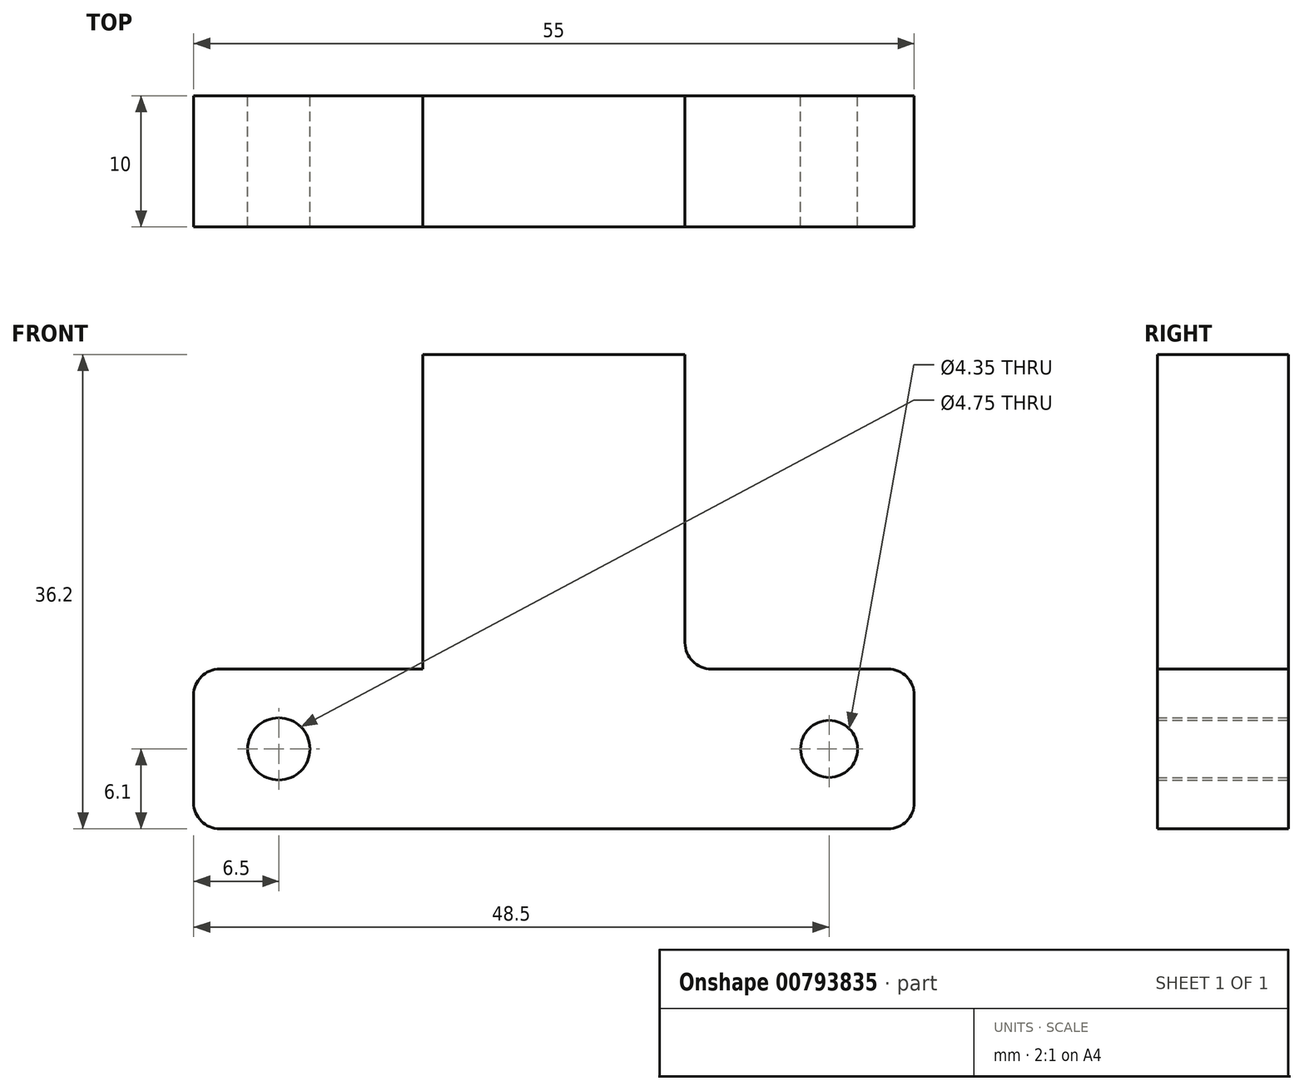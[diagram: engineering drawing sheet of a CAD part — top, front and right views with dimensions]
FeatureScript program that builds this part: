
annotation { "Feature Type Name" : "Feature", "Feature Type Description" : "" }
export const myFeature = defineFeature(function(context is Context, id is Id, definition is map)
    precondition{}
    {
        {
            var Q0;
            Q0=qCreatedBy(makeId("Front.planeOp"),FACE);
            var sketch = newSketch(context, id + "F0", { "sketchPlane" : qUnion([Q0])});
            skLineSegment(sketch, "E0.bottom", {"start": v(-27.5, 6.1) * mm, "end": v(27.5, 6.1) * mm});
            skLineSegment(sketch, "E0.top", {"start": v(-27.5, -6.1) * mm, "end": v(27.5, -6.1) * mm});
            skLineSegment(sketch, "E0.left", {"start": v(-27.5, 6.1) * mm, "end": v(-27.5, -6.1) * mm});
            skLineSegment(sketch, "E0.right", {"start": v(27.5, 6.1) * mm, "end": v(27.5, -6.1) * mm});
            skCircle(sketch, "E1", {"center": v(21, 0) * mm, "radius": 2.18 * mm});
            skCircle(sketch, "E2", {"center": v(-21, 0) * mm, "radius": 2.37 * mm});
            skSolve(sketch);
        }
        {
            var Q0;
            Q0=qSketchRegion(id+"F0",true);
            extrude(context, id + "F1", {"entities" : qUnion([Q0]), "depth" : 10 * mm, "offsetDistance" : 25 * mm});
        }
        {
            var Q0;
            Q0=makeQuery(id+"F1.opExtrude","SWEPT_FACE",FACE,{"disambiguationData":[OSD([sQuery(id+"F0.wireOp",EDGE,"E0.bottom")])]});
            var sketch = newSketch(context, id + "F2", { "sketchPlane" : qUnion([Q0])});
            skLineSegment(sketch, "E3.bottom", {"start": v(-10, 0) * mm, "end": v(10, 0) * mm});
            skLineSegment(sketch, "E3.top", {"start": v(-10, -10) * mm, "end": v(10, -10) * mm});
            skLineSegment(sketch, "E3.left", {"start": v(-10, 0) * mm, "end": v(-10, -10) * mm});
            skLineSegment(sketch, "E3.right", {"start": v(10, 0) * mm, "end": v(10, -10) * mm});
            skSolve(sketch);
        }
        {
            var Q0;
            Q0=qSketchRegion(id+"F2",true);
            extrude(context, id + "F3", {"entities" : qUnion([Q0]), "operationType" : NewBodyOperationType.ADD, "depth" : 24 * mm, "offsetDistance" : 25 * mm});
        }
        {
            var Q0;
            Q0=makeQuery(id+"F3.opExtrude","CAP_EDGE",EDGE,{"disambiguationData":[OSD([sQuery(id+"F2.wireOp",EDGE,"E3.right")])],"isStart":true});
            var Q1;
            Q1=makeQuery(id+"F1.opExtrude","SWEPT_EDGE",EDGE,{"disambiguationData":[OSD([sQuery(id+"F0.wireOp",EDGE,"E0.bottom"),sQuery(id+"F0.wireOp",EDGE,"E0.right")])]});
            var Q2;
            Q2=makeQuery(id+"F1.opExtrude","SWEPT_EDGE",EDGE,{"disambiguationData":[OSD([sQuery(id+"F0.wireOp",EDGE,"E0.top"),sQuery(id+"F0.wireOp",EDGE,"E0.right")])]});
            var Q3;
            {var subQ0=sQuery(id+"F2.wireOp",EDGE,"E3.right");Q3=makeQuery(id+"FlKPv2pDkQqTPje_1.opChamfer","BLEND_EDGE",EDGE,{"blendedFrom":[makeQuery(id+"F3.opExtrude","CAP_EDGE",EDGE,{"disambiguationData":[OSD([subQ0])],"isStart":false}),makeQuery(id+"F3.opExtrude","SWEPT_FACE",FACE,{"disambiguationData":[OSD([subQ0])]})],"blendedInto":[makeQuery(id+"F3.opExtrude","SWEPT_FACE",FACE,{"disambiguationData":[OSD([subQ0])]})]});}
            var Q4;
            {var subQ0=sQuery(id+"F2.wireOp",EDGE,"E3.left");Q4=makeQuery(id+"FlKPv2pDkQqTPje_1.opChamfer","BLEND_EDGE",EDGE,{"blendedFrom":[makeQuery(id+"F3.opExtrude","CAP_EDGE",EDGE,{"disambiguationData":[OSD([subQ0])],"isStart":false}),makeQuery(id+"F3.opExtrude","SWEPT_FACE",FACE,{"disambiguationData":[OSD([subQ0])]})],"blendedInto":[makeQuery(id+"F3.opExtrude","SWEPT_FACE",FACE,{"disambiguationData":[OSD([subQ0])]})]});}
            var Q5;
            Q5=makeQuery(id+"F3.opExtrude","CAP_EDGE",EDGE,{"disambiguationData":[OSD([sQuery(id+"F2.wireOp",EDGE,"E3.left")])],"isStart":true});
            var Q6;
            Q6=makeQuery(id+"F1.opExtrude","SWEPT_EDGE",EDGE,{"disambiguationData":[OSD([sQuery(id+"F0.wireOp",EDGE,"E0.bottom"),sQuery(id+"F0.wireOp",EDGE,"E0.left")])]});
            var Q7;
            Q7=makeQuery(id+"F1.opExtrude","SWEPT_EDGE",EDGE,{"disambiguationData":[OSD([sQuery(id+"F0.wireOp",EDGE,"E0.top"),sQuery(id+"F0.wireOp",EDGE,"E0.left")])]});
            fillet(context, id + "F4", {"entities" : qUnion([Q0, Q1, Q2, Q3, Q4, Q5, Q6, Q7]), "radius" : 2 * mm, "tangentPropagation" : true, "allowEdgeOverflow" : false});
        }
    });
